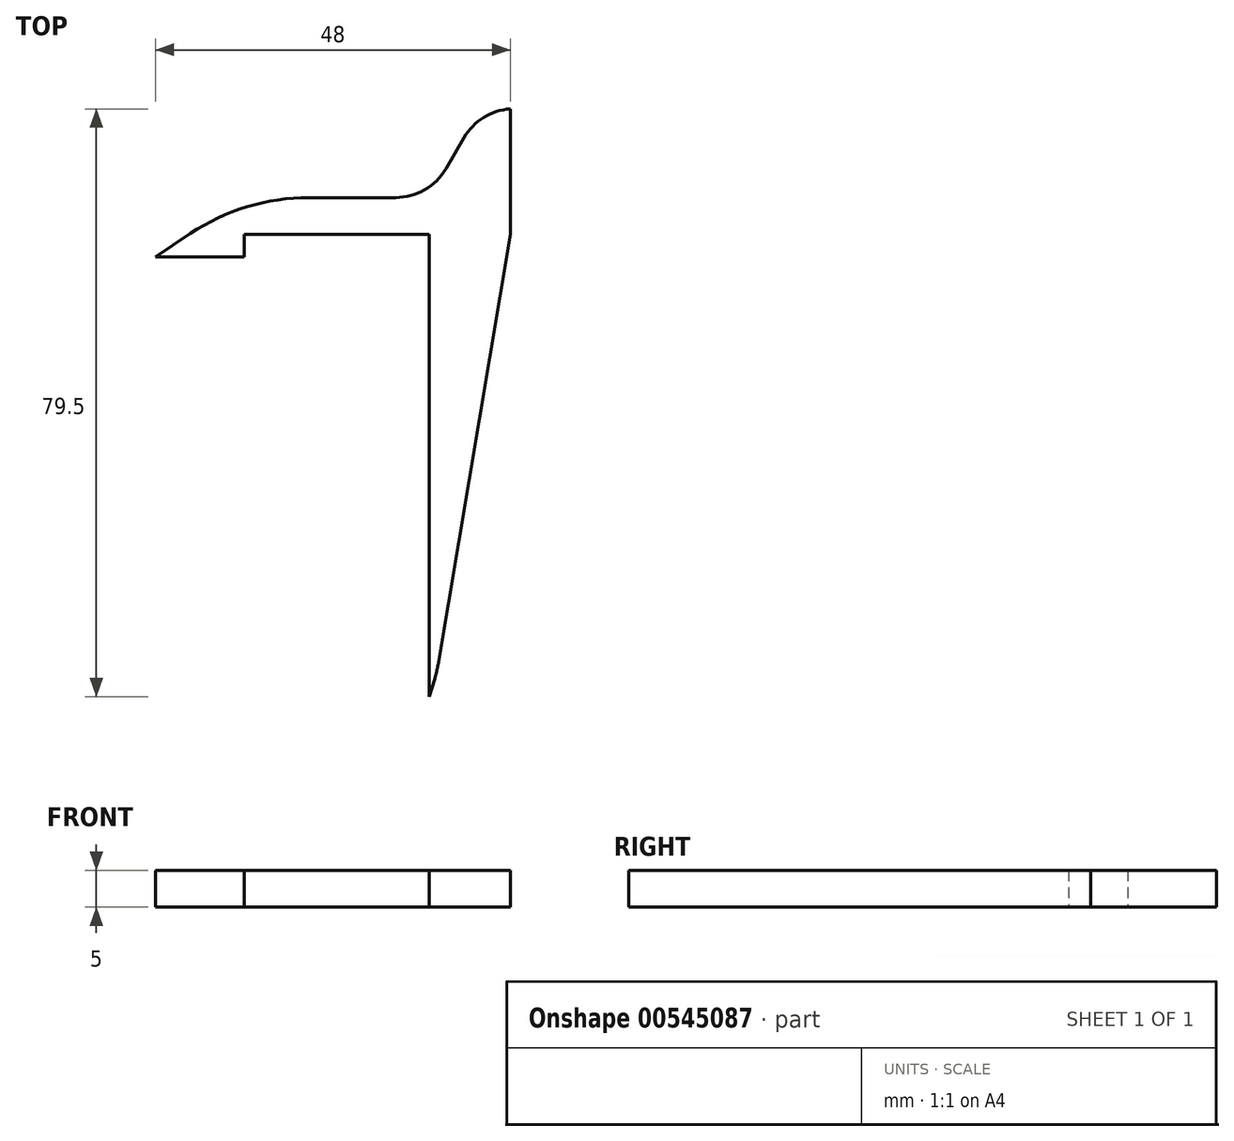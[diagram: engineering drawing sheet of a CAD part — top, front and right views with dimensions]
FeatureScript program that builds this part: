
annotation { "Feature Type Name" : "Feature", "Feature Type Description" : "" }
export const myFeature = defineFeature(function(context is Context, id is Id, definition is map)
    precondition{}
    {
        {
            var Q0;
            Q0=qCreatedBy(makeId("Top.planeOp"),FACE);
            var sketch = newSketch(context, id + "F0", { "sketchPlane" : qUnion([Q0])});
            skLineSegment(sketch, "E0", {"start": v(0, 0) * mm, "end": v(0, -62.5) * mm});
            skLineSegment(sketch, "E1", {"start": v(0, 0) * mm, "end": v(-25, 0) * mm});
            skLineSegment(sketch, "E2", {"start": v(-25, 0) * mm, "end": v(-25, -3) * mm});
            skLineSegment(sketch, "E3", {"start": v(-25, -3) * mm, "end": v(-37, -3) * mm});
            skLineSegment(sketch, "E4", {"start": v(-25, 5) * mm, "end": v(0, 5) * mm});
            skLineSegment(sketch, "E5", {"start": v(-37, -3) * mm, "end": v(-25, 5) * mm});
            skLineSegment(sketch, "E6", {"start": v(11, 0) * mm, "end": v(1.04, -59.17) * mm});
            skLineSegment(sketch, "E7", {"start": v(1.04, -59.17) * mm, "end": v(0, -62.5) * mm});
            skLineSegment(sketch, "E8", {"start": v(11, 0) * mm, "end": v(11, 17) * mm});
            skLineSegment(sketch, "E9", {"start": v(11, 17) * mm, "end": v(7, 17) * mm});
            skLineSegment(sketch, "E10", {"start": v(7, 17) * mm, "end": v(0, 5) * mm});
            skSolve(sketch);
        }
        {
            var Q0;
            Q0=makeQuery(id+"F0.imprint","IMPRINT",FACE,{"disambiguationData":[TD([[makeQuery(id+"F0.imprint","IMPRINT",EDGE,{"derivedFrom":sQuery(id+"F0.wireOp",EDGE,"E0")}),1.0]])]});
            extrude(context, id + "F1", {"entities" : qUnion([Q0]), "depth" : 5 * mm, "offsetDistance" : 25 * mm});
        }
        {
            var Q0;
            Q0=makeQuery(id+"F1.opExtrude","SWEPT_EDGE",EDGE,{"disambiguationData":[OSD([sQuery(id+"F0.wireOp",EDGE,"E4"),sQuery(id+"F0.wireOp",EDGE,"E10")])]});
            var Q1;
            Q1=makeQuery(id+"F1.opExtrude","SWEPT_EDGE",EDGE,{"disambiguationData":[OSD([sQuery(id+"F0.wireOp",EDGE,"E9"),sQuery(id+"F0.wireOp",EDGE,"E10")])]});
            fillet(context, id + "F2", {"entities" : qUnion([Q0, Q1]), "radius" : 7.86 * mm, "tangentPropagation" : true, "allowEdgeOverflow" : false});
        }
        {
            var Q0;
            Q0=makeQuery(id+"F1.opExtrude","SWEPT_EDGE",EDGE,{"disambiguationData":[OSD([sQuery(id+"F0.wireOp",EDGE,"E4"),sQuery(id+"F0.wireOp",EDGE,"E5")])]});
            fillet(context, id + "F3", {"entities" : qUnion([Q0]), "radius" : 29 * mm, "tangentPropagation" : true, "allowEdgeOverflow" : false});
        }
        {
            var Q0;
            Q0=makeQuery(id+"F1.opExtrude","SWEPT_EDGE",EDGE,{"disambiguationData":[OSD([sQuery(id+"F0.wireOp",EDGE,"E6"),sQuery(id+"F0.wireOp",EDGE,"E7")])]});
            fillet(context, id + "F4", {"entities" : qUnion([Q0]), "radius" : 14.4 * mm, "tangentPropagation" : true, "allowEdgeOverflow" : false});
        }
    });
